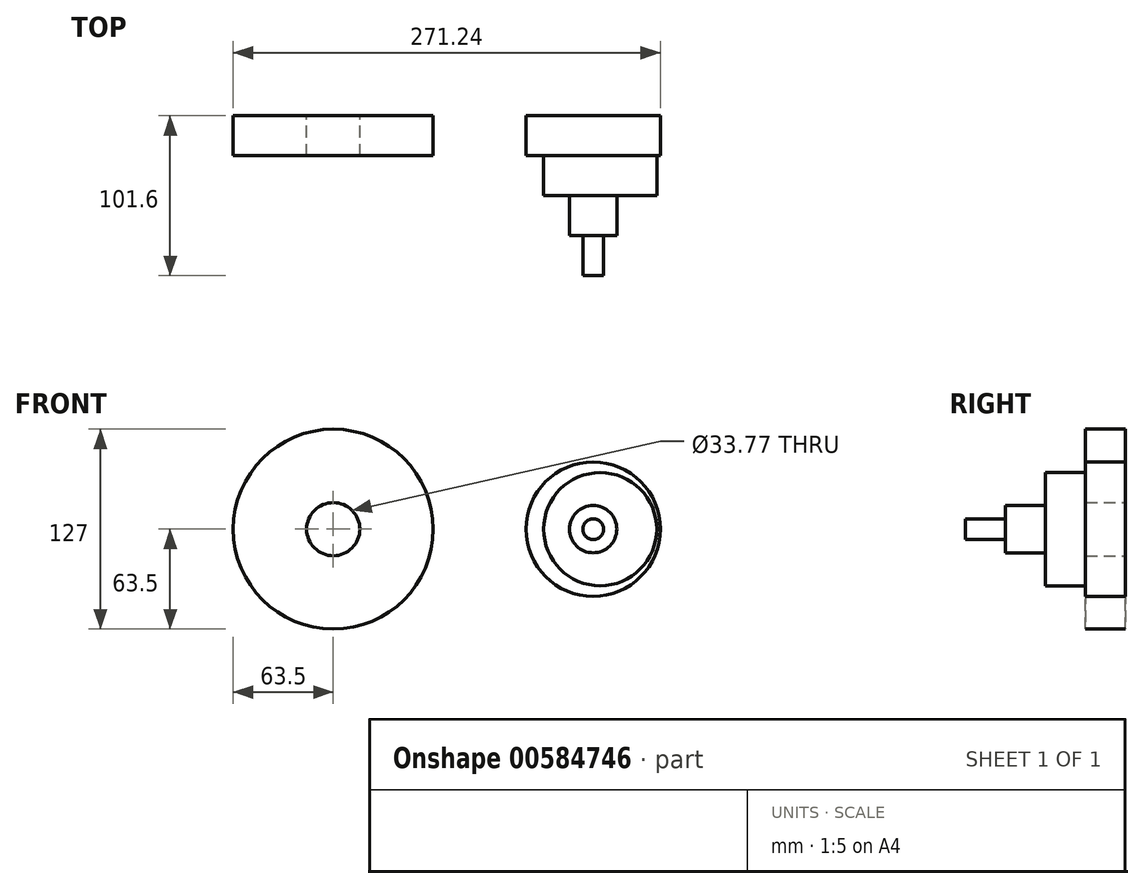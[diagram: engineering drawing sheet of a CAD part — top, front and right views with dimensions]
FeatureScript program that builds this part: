
annotation { "Feature Type Name" : "Feature", "Feature Type Description" : "" }
export const myFeature = defineFeature(function(context is Context, id is Id, definition is map)
    precondition{}
    {
        {
            var Q0;
            Q0=qCreatedBy(makeId("Front.planeOp"),FACE);
            var sketch = newSketch(context, id + "F0", { "sketchPlane" : qUnion([Q0])});
            skCircle(sketch, "E0", {"center": v(0, 0) * mm, "radius": 63.5 * mm});
            skCircle(sketch, "E1", {"center": v(165.1, 0) * mm, "radius": 42.64 * mm});
            skSolve(sketch);
        }
        {
            var Q0;
            Q0=makeQuery(id+"F0.imprint","IMPRINT",FACE,{"disambiguationData":[TD([[makeQuery(id+"F0.imprint","IMPRINT",EDGE,{"derivedFrom":sQuery(id+"F0.wireOp",EDGE,"E0")}),1.0]])]});
            var sketch = newSketch(context, id + "F1", { "sketchPlane" : qUnion([Q0])});
            skCircle(sketch, "E2", {"center": v(0, 0) * mm, "radius": 16.88 * mm});
            skCircle(sketch, "E3", {"center": v(165.6, 0.88) * mm, "radius": 13.93 * mm});
            skSolve(sketch);
        }
        {
            var Q0;
            Q0=makeQuery(id+"F0.imprint","IMPRINT",FACE,{"disambiguationData":[TD([[makeQuery(id+"F0.imprint","IMPRINT",EDGE,{"derivedFrom":sQuery(id+"F0.wireOp",EDGE,"E1")}),1.0]])]});
            var Q1;
            Q1=makeQuery(id+"F1.imprint","IMPRINT",FACE,{"disambiguationData":[TD([[makeQuery(id+"F1.imprint","IMPRINT",EDGE,{"derivedFrom":sQuery(id+"F1.wireOp",EDGE,"E2")}),-1.0]])]});
            var Q2;
            Q2 = qSketchRegion(id + "F0", true);
            extrude(context, id + "F2", {"entities" : qUnion([Q0, Q1, Q2]), "depth" : 25.4 * mm, "offsetDistance" : 25.4 * mm});
        }
        {
            var Q0;
            Q0=makeQuery(id+"F2.opExtrude","CAP_FACE",FACE,{"disambiguationData":[OSD([sQuery(id+"F0.wireOp",EDGE,"E1")])],"isStart":false});
            var sketch = newSketch(context, id + "F3", { "sketchPlane" : qUnion([Q0])});
            skCircle(sketch, "E4", {"center": v(165.1, 0) * mm, "radius": 15 * mm});
            skCircle(sketch, "E5", {"center": v(169.53, 0) * mm, "radius": 35.93 * mm});
            skSolve(sketch);
        }
        {
            var Q0;
            Q0 = qSketchRegion(id + "F3", true);
            extrude(context, id + "F4", {"entities" : qUnion([Q0]), "operationType" : NewBodyOperationType.ADD, "depth" : 25.4 * mm, "offsetDistance" : 25.4 * mm});
        }
        {
            var Q0;
            Q0=makeQuery(id+"F4.boolean.opBoolean","SPLIT",FACE,{"disambiguationData":[TD([makeQuery(id+"F4.opExtrude","SWEPT_FACE",FACE,{"disambiguationData":[OSD([sQuery(id+"F3.wireOp",EDGE,"E4")])]})])],"derivedFrom":makeQuery(id+"F2.opExtrude","CAP_FACE",FACE,{"disambiguationData":[OSD([sQuery(id+"F0.wireOp",EDGE,"E1")])],"isStart":false})});
            extrude(context, id + "F5", {"entities" : qUnion([Q0]), "operationType" : NewBodyOperationType.ADD, "depth" : 50.8 * mm, "offsetDistance" : 25.4 * mm});
        }
        {
            var Q0;
            Q0=makeQuery(id+"F5.opExtrude","CAP_FACE",FACE,{"disambiguationData":[OSD([sQuery(id+"F0.wireOp",EDGE,"E1")])],"isStart":false});
            var sketch = newSketch(context, id + "F6", { "sketchPlane" : qUnion([Q0])});
            skCircle(sketch, "E6", {"center": v(165.1, 0) * mm, "radius": 6.55 * mm});
            skSolve(sketch);
        }
        {
            var Q0;
            Q0 = qSketchRegion(id + "F6", true);
            var Q1;
            Q1=makeQuery(id+"F6.imprint","IMPRINT",FACE,{"disambiguationData":[TD([[makeQuery(id+"F6.imprint","IMPRINT",EDGE,{"derivedFrom":sQuery(id+"F6.wireOp",EDGE,"E6")}),1.0]])]});
            extrude(context, id + "F7", {"entities" : qUnion([Q0, Q1]), "operationType" : NewBodyOperationType.ADD, "depth" : 25.4 * mm, "offsetDistance" : 25.4 * mm});
        }
    });
